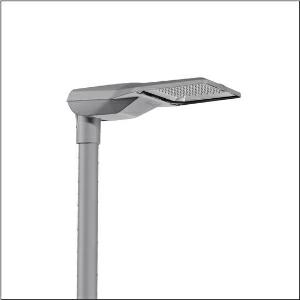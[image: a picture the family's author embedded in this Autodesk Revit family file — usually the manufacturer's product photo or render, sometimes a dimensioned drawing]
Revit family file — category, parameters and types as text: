
# Revit family: streetlight_sl_21_iq_midi___st1_0a_5xe3d31d08mb_825e
name_source: partatom
category: Lighting Fixtures
units: mm (PartAtom-declared; Revit-internal decimal feet)

## family parameters
Cut with Voids When Loaded = No
Host = Face
Light Source = No
Part Type = Normal
Room Calculation Point = No
Round Connector Dimension = Use Diameter
Shared = No

## types (1)
- --- (1 x LED, 19500 lm, 146.7 W, 3000K)
    Apparent Load = 147 VA
    CIE Flux Codes = 37 72 97 100 100
    Color Rendering = 70
    Color Temperature = 3000K
    Default Elevation = 1800 mm
    Description = Streetlight SL 21 iQ midi, mast luminaire, primary light control with lens, of PMMA, primary optical cover: cover, of toughened safety glass, transparent, light distribution: ST1.0a, light emission: direct distribution, primary light characteristic: asymmetric, installation type: post-top, side-entry, LED, High Power LED, rated luminous flux: 19.500lm, luminous efficacy: 133lm/W, light colour: 730, colour temperature: 3000K, control: Auto-Match, Temp-Guard, Lumen-Switch, Night-Set, Smart-Wire, Light-Fading, Desk-Remote (wireless, voltage-free reading and setting of iQ features in the workshop via application-optimized NFC function/RFID function), optimised constant luminous flux control (CLO 2.0), presetting dimming linear, mains connection: 230..240V, AC, 50/60Hz, start of lifetime: 147W, end of service life: 161W, reduction: 62W, luminaire housing, of diecast aluminium, powder-coated, Siteco® metallic grey (DB 702S), corrosivity category C5 mid according to DIN EN ISO 12944, please order mast flange separately, inclination adjustable: 0°, 5°, 10°, 15°, sealing non-destructively replaceable, multi-level sealing system, length: 644mm, width: 335mm, height: 110mm, mast flange for spigot size: 42mm (side-entry): 5XC10008XM4, 60/48mm (side-entry/post-top): 5XC10108XM2, 76/60mm (side-entry/post-top): 5XC10108XM1, protection rating (complete): IP66, insulation class (complete): insulation class II (safety insulation), certification: CE, ENEC, ENEC+, VDE, impact resistance: IK09, permissible operating ambient temperature for outdoor applications: -40..+50°C, standard-compliant lighting for roads and squares, packaging unit: 1 piece

Light Distribution: ST1.0a
    Height = 111 mm
    Lamp = 1 x LED
    Lamp Light Flux = 19500 lm
    Lamp Power = 146.7 W
    Lamp count = 1
    Length = 644 mm
    Luminous efficacy = 133 lm/W
    Manufacturer = Siteco
    ModVariant = No
    Model = 5XE3D31D08MB
    Number of Poles = 1
    OnlyDefault = Yes
    Power Factor = 1
    Product Name = Streetlight SL 21 iQ midi | ST1.0a
    Product group = mast luminaire | pylon top
    ProductGroupID = 6100
    Protection Class = Protection class II
    Protection Degree = IP 66
    RLX_Detail_Level = 1
    RLX_Emergency_Light_Flux = 0 lm
    RLX_Emergency_Type = 0
    RLX_Emergency_Type_DB = No
    RlxData = <blob elided: 90981 chars, md5=9907430f>
    Socket = socket
    Standby Power = 0 W
    System Light Flux = 19499 lm
    System Power = 147 W
    Type Comments = factory setting: luminous flux: 100 % | dim-lin: 254 | 753 mA
    Type Image = l_1004298.jpg
    URL = http://relux.com
    VarID = @adj_123525
    Voltage = 0 V
    Weight = 0.00 kg
    Width = 336 mm

## geometry (parser evidence)
native form markers: Blend x4, Sweep x11
no freeform markers — native parametric forms only
